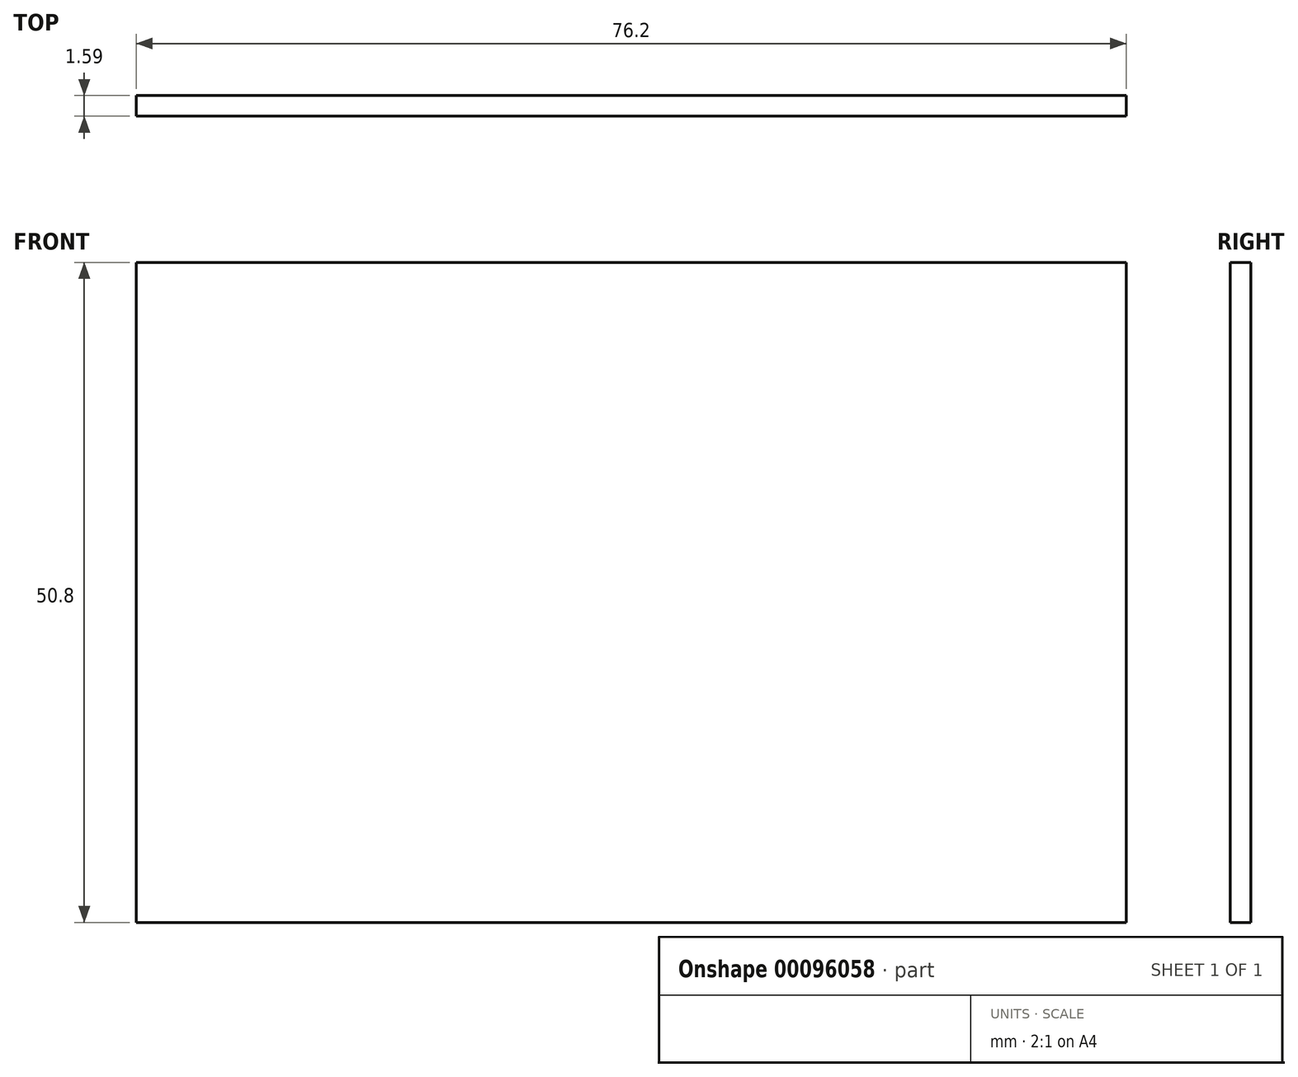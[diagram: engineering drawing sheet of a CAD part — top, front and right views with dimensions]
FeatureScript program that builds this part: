
annotation { "Feature Type Name" : "Feature", "Feature Type Description" : "" }
export const myFeature = defineFeature(function(context is Context, id is Id, definition is map)
    precondition{}
    {
        {
            var Q0;
            Q0=qCreatedBy(makeId("Front.planeOp"),FACE);
            var sketch = newSketch(context, id + "F0", { "sketchPlane" : qUnion([Q0])});
            skLineSegment(sketch, "E0.bottom", {"start": v(0, 0) * mm, "end": v(76.2, 0) * mm});
            skLineSegment(sketch, "E0.top", {"start": v(0, 50.8) * mm, "end": v(76.2, 50.8) * mm});
            skLineSegment(sketch, "E0.left", {"start": v(0, 0) * mm, "end": v(0, 50.8) * mm});
            skLineSegment(sketch, "E0.right", {"start": v(76.2, 0) * mm, "end": v(76.2, 50.8) * mm});
            skSolve(sketch);
        }
        {
            var Q0;
            Q0=makeQuery(id+"F0.imprint","IMPRINT",FACE,{"disambiguationData":[TD([[makeQuery(id+"F0.imprint","IMPRINT",EDGE,{"derivedFrom":sQuery(id+"F0.wireOp",EDGE,"E0.bottom")}),1.0]])]});
            extrude(context, id + "F1", {"entities" : qUnion([Q0]), "depth" : 1.59 * mm});
        }
    });
